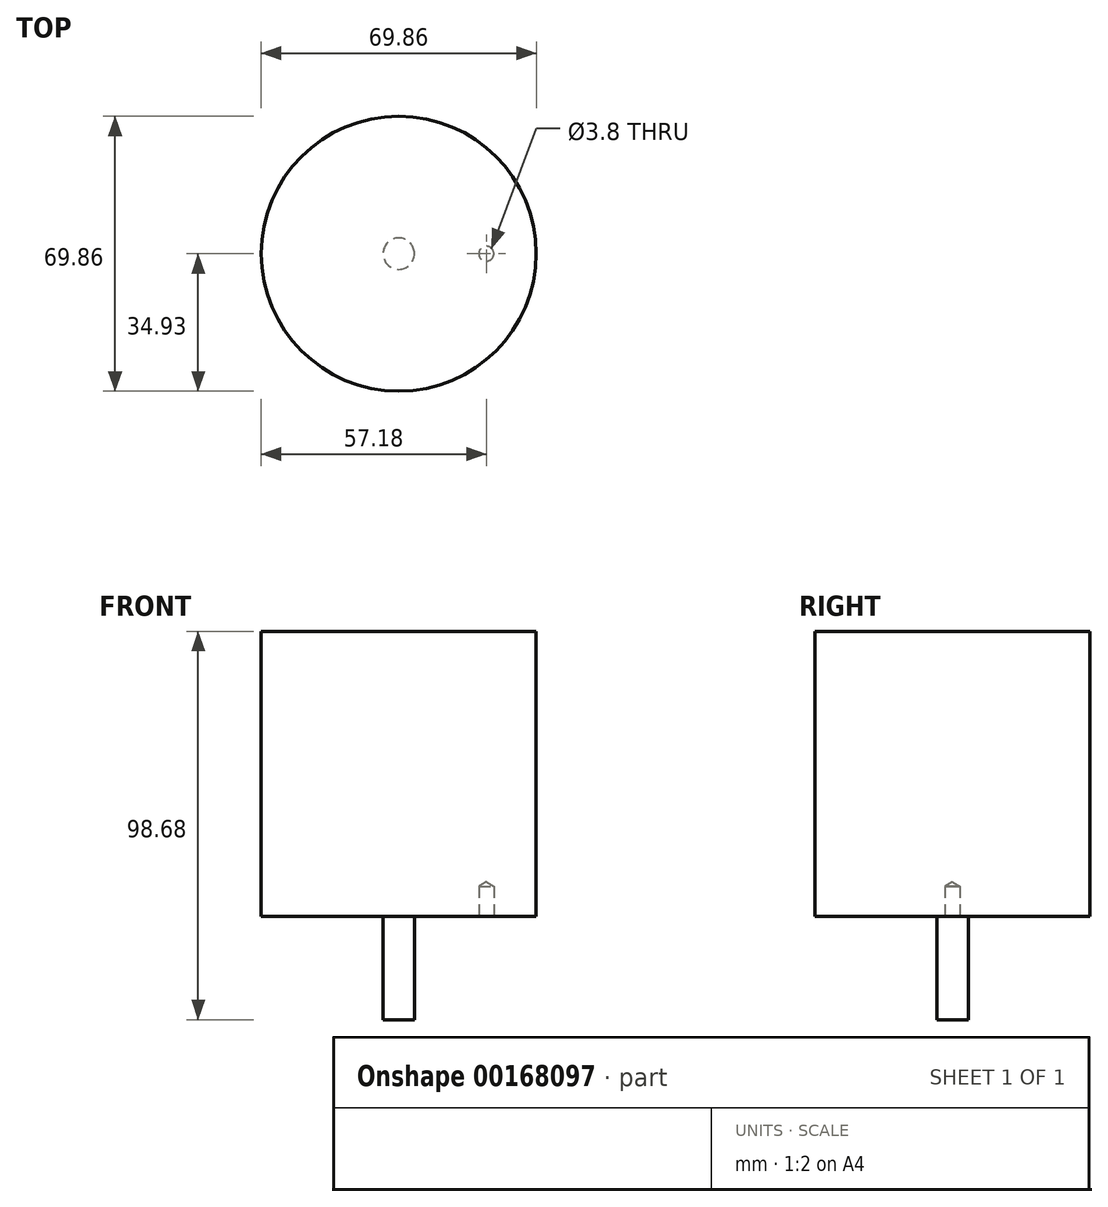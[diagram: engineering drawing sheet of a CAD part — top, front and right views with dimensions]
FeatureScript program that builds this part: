
annotation { "Feature Type Name" : "Feature", "Feature Type Description" : "" }
export const myFeature = defineFeature(function(context is Context, id is Id, definition is map)
    precondition{}
    {
        {
            var Q0;
            Q0=qCreatedBy(makeId("Top.planeOp"),FACE);
            var sketch = newSketch(context, id + "F0", { "sketchPlane" : qUnion([Q0])});
            skCircle(sketch, "E0", {"center": v(0, 0) * mm, "radius": 34.93 * mm});
            skSolve(sketch);
        }
        {
            var Q0;
            Q0=qSketchRegion(id+"F0",true);
            extrude(context, id + "F1", {"entities" : qUnion([Q0]), "depth" : 72.39 * mm});
        }
        {
            var Q0;
            Q0=makeQuery(id+"F1.opExtrude","CAP_FACE",FACE,{"disambiguationData":[OSD([sQuery(id+"F0.wireOp",EDGE,"E0")])],"isStart":true});
            var sketch = newSketch(context, id + "F2", { "sketchPlane" : qUnion([Q0])});
            skCircle(sketch, "E1", {"center": v(0, 0) * mm, "radius": 3.99 * mm});
            skSolve(sketch);
        }
        {
            var Q0;
            Q0=qSketchRegion(id+"F2",true);
            extrude(context, id + "F3", {"entities" : qUnion([Q0]), "operationType" : NewBodyOperationType.ADD, "depth" : 26.29 * mm});
        }
        {
            var Q0;
            Q0=makeQuery(id+"F1.opExtrude","CAP_FACE",FACE,{"disambiguationData":[OSD([sQuery(id+"F0.wireOp",EDGE,"E0")])],"isStart":true});
            var sketch = newSketch(context, id + "F4", { "sketchPlane" : qUnion([Q0])});
            skPoint(sketch, "E2", {"position": v(22.25, 0) * mm});
            skSolve(sketch);
        }
        {
            var Q0;
            Q0=sQuery(id+"F4.wireOp",VERTEX,"E2");
            var Q1;
            Q1=makeQuery(id+"F1.opExtrude","SWEPT_BODY",BODY,{"disambiguationData":[OSD([sQuery(id+"F0.wireOp",EDGE,"E0")])]});
            hole(context, id + "F5", {"style" : HoleStyle.SIMPLE, "endStyle" : HoleEndStyle.BLIND, "standardTappedOrClearance" : lookupTablePath({ "standard" : "ANSI", "engagement" : "75%", "pitch" : "24 tpi", "size" : "#10", "type" : "Tapped" }), "standardBlindInLast" : lookupTablePath({ "standard" : "ANSI", "engagement" : "75%", "pitch" : "24 tpi", "size" : "#10", "type" : "Tapped" }), "holeDiameter" : 3.8 * mm, "holeDepth" : 7.62 * mm, "locations" : qUnion([Q0]), "scope" : qUnion([Q1]), "majorDiameter" : 4.83 * mm});
        }
        {
            var Q0;
            Q0=qCreatedBy(makeId("Front.planeOp"),FACE);
            var sketch = newSketch(context, id + "F6", { "sketchPlane" : qUnion([Q0])});
            skLineSegment(sketch, "E3", {"start": v(0, 0) * mm, "end": v(0, -23.14) * mm, "construction": true});
            skSolve(sketch);
        }
    });
